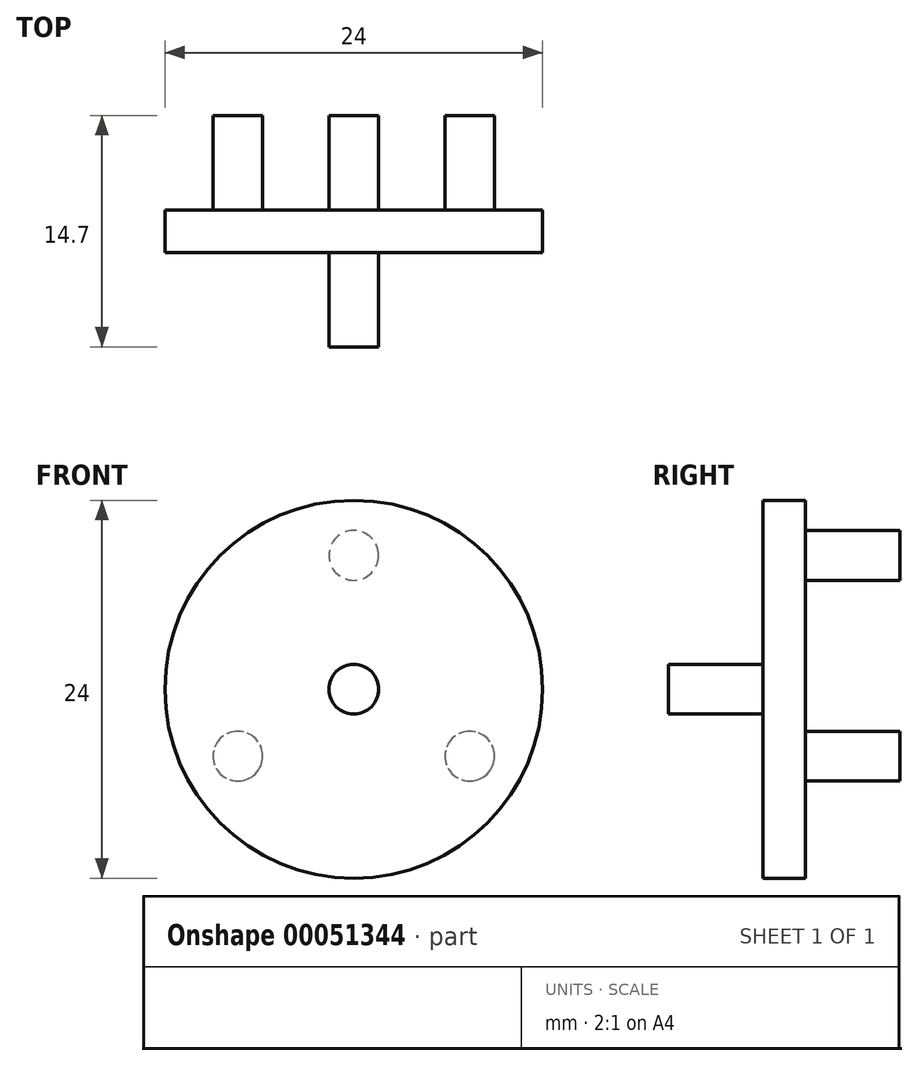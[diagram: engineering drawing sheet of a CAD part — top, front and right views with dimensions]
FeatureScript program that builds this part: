
annotation { "Feature Type Name" : "Feature", "Feature Type Description" : "" }
export const myFeature = defineFeature(function(context is Context, id is Id, definition is map)
    precondition{}
    {
        {
            var Q0;
            Q0=qCreatedBy(makeId("Front.planeOp"),FACE);
            var sketch = newSketch(context, id + "F0", { "sketchPlane" : qUnion([Q0])});
            skCircle(sketch, "E0", {"center": v(0, 0) * mm, "radius": 12 * mm});
            skSolve(sketch);
        }
        {
            var Q0;
            Q0 = qSketchRegion(id + "F0", true);
            extrude(context, id + "F1", {"entities" : qUnion([Q0]), "depth" : 2.7 * mm, "symmetric" : true});
        }
        {
            var Q0;
            Q0=makeQuery(id+"F1.opExtrude","CAP_FACE",FACE,{"disambiguationData":[OSD([sQuery(id+"F0.wireOp",EDGE,"E0")])],"isStart":false});
            var sketch = newSketch(context, id + "F2", { "sketchPlane" : qUnion([Q0])});
            skCircle(sketch, "E1", {"center": v(0, 0) * mm, "radius": 1.58 * mm});
            skSolve(sketch);
        }
        {
            var Q0;
            Q0 = qSketchRegion(id + "F2", true);
            extrude(context, id + "F3", {"entities" : qUnion([Q0]), "operationType" : NewBodyOperationType.ADD, "depth" : 6 * mm});
        }
        {
            var Q0;
            Q0=makeQuery(id+"F1.opExtrude","CAP_FACE",FACE,{"disambiguationData":[OSD([sQuery(id+"F0.wireOp",EDGE,"E0")])],"isStart":true});
            var sketch = newSketch(context, id + "F4", { "sketchPlane" : qUnion([Q0])});
            skLineSegment(sketch, "E2", {"start": v(0, 0) * mm, "end": v(0, 12) * mm, "construction": true});
            skCircle(sketch, "E3", {"center": v(0, 8.5) * mm, "radius": 1.58 * mm});
            skCircle(sketch, "E4.1.0", {"center": v(-7.36, -4.25) * mm, "radius": 1.58 * mm});
            skCircle(sketch, "E4.2.0", {"center": v(7.36, -4.25) * mm, "radius": 1.58 * mm});
            skPoint(sketch, "E4.center", {"position": v(0, 0) * mm});
            skSolve(sketch);
        }
        {
            var Q0;
            Q0 = qSketchRegion(id + "F4", true);
            extrude(context, id + "F5", {"entities" : qUnion([Q0]), "operationType" : NewBodyOperationType.ADD, "depth" : 6 * mm});
        }
    });
